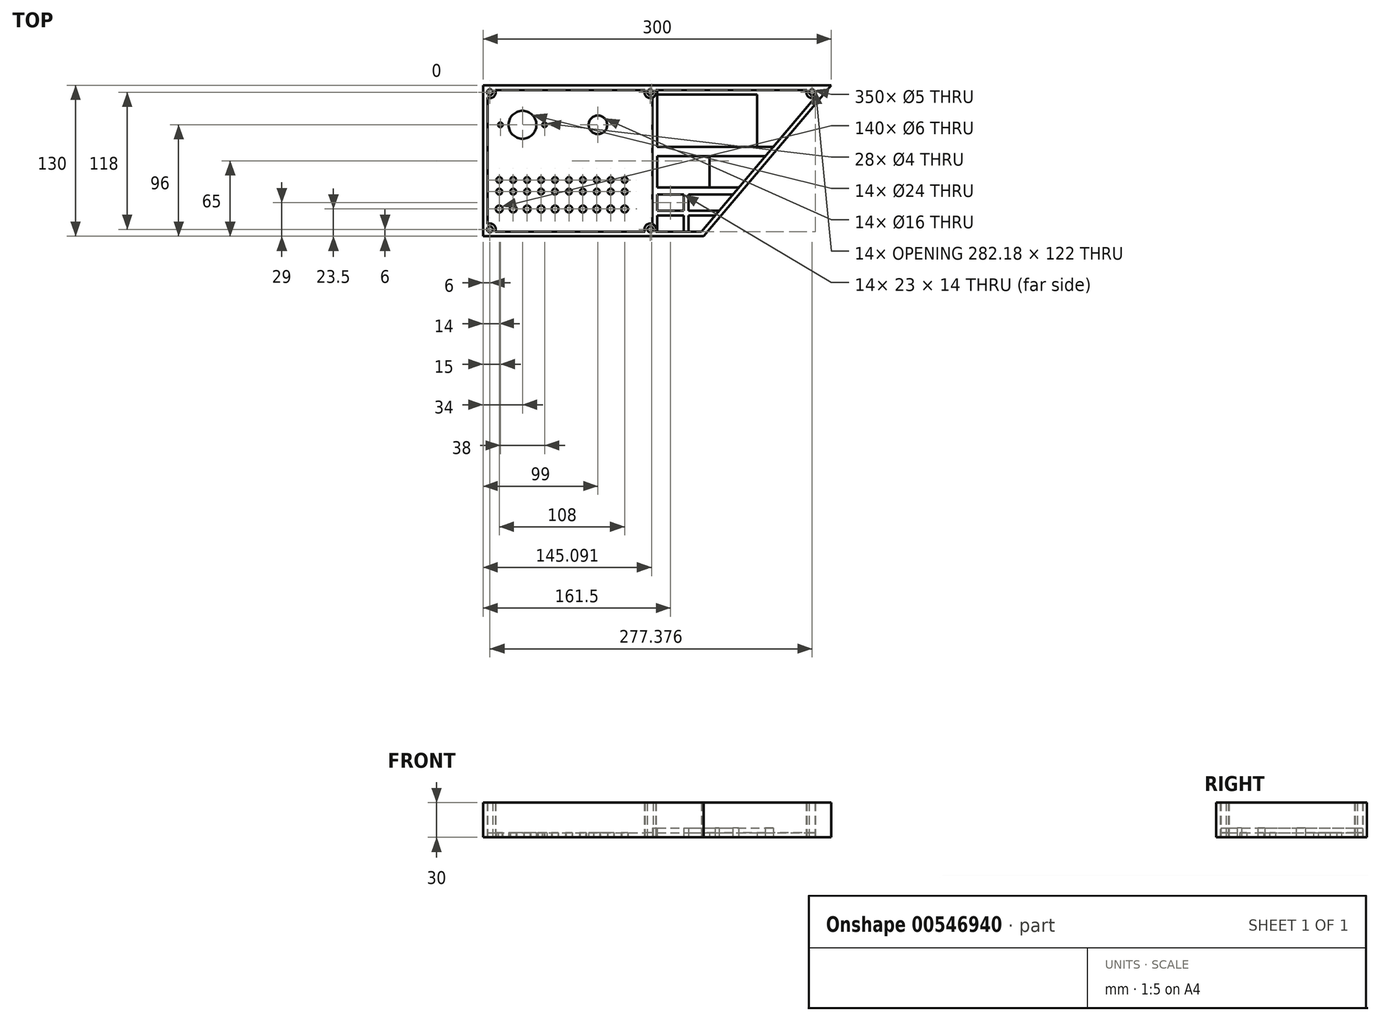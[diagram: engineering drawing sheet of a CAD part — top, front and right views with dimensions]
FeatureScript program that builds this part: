
annotation { "Feature Type Name" : "Feature", "Feature Type Description" : "" }
export const myFeature = defineFeature(function(context is Context, id is Id, definition is map)
    precondition{}
    {
        {
            var Q0;
            Q0=qCreatedBy(makeId("Top.planeOp"),FACE);
            var sketch = newSketch(context, id + "F0", { "sketchPlane" : qUnion([Q0])});
            skLineSegment(sketch, "E0", {"start": v(0, 0) * mm, "end": v(190, 0) * mm});
            skLineSegment(sketch, "E1", {"start": v(0, 0) * mm, "end": v(0, 130) * mm});
            skLineSegment(sketch, "E2", {"start": v(0, 130) * mm, "end": v(300, 130) * mm});
            skLineSegment(sketch, "E3", {"start": v(300, 130) * mm, "end": v(190, 0) * mm});
            skLineSegment(sketch, "E4.0", {"start": v(236, 77) * mm, "end": v(236, 122) * mm});
            skLineSegment(sketch, "E5.trimOffspring", {"start": v(195, 42) * mm, "end": v(195, 69) * mm});
            skLineSegment(sketch, "E6.0", {"start": v(173, 4) * mm, "end": v(173, 18) * mm});
            skLineSegment(sketch, "E7.0", {"start": v(150, 122) * mm, "end": v(236, 122) * mm});
            skLineSegment(sketch, "E8.0", {"start": v(150, 77) * mm, "end": v(249.91, 77) * mm});
            skLineSegment(sketch, "E9.0", {"start": v(150, 69) * mm, "end": v(243.14, 69) * mm});
            skLineSegment(sketch, "E10.0", {"start": v(150, 42) * mm, "end": v(220.3, 42) * mm});
            skLineSegment(sketch, "E11.0", {"start": v(150, 4) * mm, "end": v(173, 4) * mm});
            skLineSegment(sketch, "E12.0", {"start": v(150, 18) * mm, "end": v(173, 18) * mm});
            skLineSegment(sketch, "E13.0", {"start": v(150, 36) * mm, "end": v(173, 36) * mm});
            skLineSegment(sketch, "E14.0", {"start": v(150, 22) * mm, "end": v(173, 22) * mm});
            skLineSegment(sketch, "E15.trimOffspring", {"start": v(173, 22) * mm, "end": v(173, 36) * mm});
            skLineSegment(sketch, "E16.0", {"start": v(10.58, 126) * mm, "end": v(139.42, 126) * mm});
            skLineSegment(sketch, "E17.0", {"start": v(286.18, 119.86) * mm, "end": v(188.14, 4) * mm});
            skLineSegment(sketch, "E18.0", {"start": v(10.58, 4) * mm, "end": v(139.42, 4) * mm});
            skLineSegment(sketch, "E19.0", {"start": v(4, 10.58) * mm, "end": v(4, 119.42) * mm});
            skLineSegment(sketch, "E20", {"start": v(150, 4) * mm, "end": v(150, 126) * mm});
            skLineSegment(sketch, "E21.0", {"start": v(146, 10.58) * mm, "end": v(146, 119.42) * mm});
            skLineSegment(sketch, "E22.0", {"start": v(177, 22) * mm, "end": v(177, 36) * mm});
            skLineSegment(sketch, "E23.0", {"start": v(177, 4) * mm, "end": v(177, 18) * mm});
            skLineSegment(sketch, "E24.trimOffspring", {"start": v(177, 36) * mm, "end": v(215.22, 36) * mm});
            skLineSegment(sketch, "E25.trimOffspring", {"start": v(177, 22) * mm, "end": v(203.38, 22) * mm});
            skLineSegment(sketch, "E26.trimOffspring", {"start": v(177, 18) * mm, "end": v(200, 18) * mm});
            skLineSegment(sketch, "E27", {"start": v(10.58, 126) * mm, "end": v(34, 126) * mm, "construction": true});
            skLineSegment(sketch, "E28", {"start": v(34, 126) * mm, "end": v(34, 96) * mm, "construction": true});
            skCircle(sketch, "E29", {"center": v(34, 96) * mm, "radius": 12 * mm});
            skLineSegment(sketch, "E30.0", {"start": v(15, 126) * mm, "end": v(15, 96) * mm, "construction": true});
            skLineSegment(sketch, "E31.0", {"start": v(53, 126) * mm, "end": v(53, 96) * mm, "construction": true});
            skCircle(sketch, "E32", {"center": v(15, 96) * mm, "radius": 2 * mm});
            skCircle(sketch, "E33", {"center": v(53, 96) * mm, "radius": 2 * mm});
            skCircle(sketch, "E34", {"center": v(34, 96) * mm, "radius": 30 * mm, "construction": true});
            skLineSegment(sketch, "E35.0", {"start": v(4, 23.5) * mm, "end": v(146, 23.5) * mm, "construction": true});
            skLineSegment(sketch, "E36.0", {"start": v(4, 38.5) * mm, "end": v(146, 38.5) * mm, "construction": true});
            skLineSegment(sketch, "E37.0", {"start": v(4, 49) * mm, "end": v(146, 49) * mm, "construction": true});
            skLineSegment(sketch, "E38", {"start": v(4, 10.58) * mm, "end": v(4, 49) * mm, "construction": true});
            skLineSegment(sketch, "E39.0", {"start": v(14, 3.5) * mm, "end": v(14, 23.5) * mm, "construction": true});
            skLineSegment(sketch, "E40.0", {"start": v(26, 3.5) * mm, "end": v(26, 23.5) * mm, "construction": true});
            skLineSegment(sketch, "E41.0", {"start": v(38, 3.5) * mm, "end": v(38, 23.5) * mm, "construction": true});
            skLineSegment(sketch, "E42.0", {"start": v(50, 3.5) * mm, "end": v(50, 23.5) * mm, "construction": true});
            skLineSegment(sketch, "E43.0", {"start": v(62, 3.5) * mm, "end": v(62, 23.5) * mm, "construction": true});
            skLineSegment(sketch, "E44.0", {"start": v(74, 3.5) * mm, "end": v(74, 23.5) * mm, "construction": true});
            skLineSegment(sketch, "E45.0", {"start": v(86, 3.5) * mm, "end": v(86, 23.5) * mm, "construction": true});
            skLineSegment(sketch, "E46.0", {"start": v(98, 3.5) * mm, "end": v(98, 23.5) * mm, "construction": true});
            skLineSegment(sketch, "E47.0", {"start": v(110, 3.5) * mm, "end": v(110, 23.5) * mm, "construction": true});
            skLineSegment(sketch, "E48.0", {"start": v(122, 3.5) * mm, "end": v(122, 23.5) * mm, "construction": true});
            skLineSegment(sketch, "E49.trimOffspring", {"start": v(122, 38.5) * mm, "end": v(122, 48.5) * mm, "construction": true});
            skLineSegment(sketch, "E50.trimOffspring", {"start": v(110, 38.5) * mm, "end": v(110, 48.5) * mm, "construction": true});
            skLineSegment(sketch, "E51.trimOffspring", {"start": v(98, 38.5) * mm, "end": v(98, 48.5) * mm, "construction": true});
            skLineSegment(sketch, "E52.trimOffspring", {"start": v(86, 38.5) * mm, "end": v(86, 48.5) * mm, "construction": true});
            skLineSegment(sketch, "E53.trimOffspring", {"start": v(74, 38.5) * mm, "end": v(74, 48.5) * mm, "construction": true});
            skLineSegment(sketch, "E54.trimOffspring", {"start": v(62, 38.5) * mm, "end": v(62, 48.5) * mm, "construction": true});
            skLineSegment(sketch, "E55.trimOffspring", {"start": v(50, 38.5) * mm, "end": v(50, 48.5) * mm, "construction": true});
            skLineSegment(sketch, "E56.trimOffspring", {"start": v(38, 38.5) * mm, "end": v(38, 48.5) * mm, "construction": true});
            skLineSegment(sketch, "E57.trimOffspring", {"start": v(26, 38.5) * mm, "end": v(26, 48.5) * mm, "construction": true});
            skLineSegment(sketch, "E58.trimOffspring", {"start": v(14, 38.5) * mm, "end": v(14, 48.5) * mm, "construction": true});
            skCircle(sketch, "E59", {"center": v(14, 23.5) * mm, "radius": 3 * mm});
            skCircle(sketch, "E60", {"center": v(26, 23.5) * mm, "radius": 3 * mm});
            skCircle(sketch, "E61", {"center": v(38, 23.5) * mm, "radius": 3 * mm});
            skCircle(sketch, "E62", {"center": v(50, 23.5) * mm, "radius": 3 * mm});
            skCircle(sketch, "E63", {"center": v(62, 23.5) * mm, "radius": 3 * mm});
            skCircle(sketch, "E64", {"center": v(74, 23.5) * mm, "radius": 3 * mm});
            skCircle(sketch, "E65", {"center": v(86, 23.5) * mm, "radius": 3 * mm});
            skCircle(sketch, "E66", {"center": v(98, 23.5) * mm, "radius": 3 * mm});
            skCircle(sketch, "E67", {"center": v(110, 23.5) * mm, "radius": 3 * mm});
            skCircle(sketch, "E68", {"center": v(122, 23.5) * mm, "radius": 3 * mm});
            skCircle(sketch, "E69", {"center": v(14, 38.5) * mm, "radius": 2.5 * mm});
            skCircle(sketch, "E70", {"center": v(26, 38.5) * mm, "radius": 2.5 * mm});
            skCircle(sketch, "E71", {"center": v(38, 38.5) * mm, "radius": 2.5 * mm});
            skCircle(sketch, "E72", {"center": v(50, 38.5) * mm, "radius": 2.5 * mm});
            skCircle(sketch, "E73", {"center": v(62, 38.5) * mm, "radius": 2.5 * mm});
            skCircle(sketch, "E74", {"center": v(74, 38.5) * mm, "radius": 2.5 * mm});
            skCircle(sketch, "E75", {"center": v(86, 38.5) * mm, "radius": 2.5 * mm});
            skCircle(sketch, "E76", {"center": v(98, 38.5) * mm, "radius": 2.5 * mm});
            skCircle(sketch, "E77", {"center": v(110, 38.5) * mm, "radius": 2.5 * mm});
            skCircle(sketch, "E78", {"center": v(122, 38.5) * mm, "radius": 2.5 * mm});
            skCircle(sketch, "E79", {"center": v(14, 48.5) * mm, "radius": 2.5 * mm});
            skCircle(sketch, "E80", {"center": v(26, 48.5) * mm, "radius": 2.5 * mm});
            skCircle(sketch, "E81", {"center": v(38, 48.5) * mm, "radius": 2.5 * mm});
            skCircle(sketch, "E82", {"center": v(50, 48.5) * mm, "radius": 2.5 * mm});
            skCircle(sketch, "E83", {"center": v(62, 48.5) * mm, "radius": 2.5 * mm});
            skCircle(sketch, "E84", {"center": v(74, 48.5) * mm, "radius": 2.5 * mm});
            skCircle(sketch, "E85", {"center": v(86, 48.5) * mm, "radius": 2.5 * mm});
            skCircle(sketch, "E86", {"center": v(98, 48.5) * mm, "radius": 2.5 * mm});
            skCircle(sketch, "E87", {"center": v(110, 48.5) * mm, "radius": 2.5 * mm});
            skCircle(sketch, "E88", {"center": v(122, 48.5) * mm, "radius": 2.5 * mm});
            skLineSegment(sketch, "E89", {"start": v(34, 96) * mm, "end": v(99, 96) * mm, "construction": true});
            skCircle(sketch, "E90", {"center": v(99, 96) * mm, "radius": 8 * mm});
            skCircle(sketch, "E91", {"center": v(6, 124) * mm, "radius": 2.5 * mm});
            skArc(sketch, "E92", {"start": v(4, 119.42) * mm, "mid": v(9.54, 120.46) * mm, "end": v(10.58, 126) * mm});
            skCircle(sketch, "E93", {"center": v(6, 6) * mm, "radius": 2.5 * mm});
            skArc(sketch, "E94", {"start": v(10.58, 4) * mm, "mid": v(9.54, 9.54) * mm, "end": v(4, 10.58) * mm});
            skLineSegment(sketch, "E95", {"start": v(146, 6) * mm, "end": v(144, 6) * mm, "construction": true});
            skCircle(sketch, "E96", {"center": v(144, 6) * mm, "radius": 2.5 * mm});
            skArc(sketch, "E97", {"start": v(148.58, 4) * mm, "mid": v(144, 11) * mm, "end": v(139.42, 4) * mm});
            skPoint(sketch, "E98.orphan", {"position": v(146, 4) * mm});
            skLineSegment(sketch, "E99.trimOffspring", {"start": v(148.58, 4) * mm, "end": v(188.14, 4) * mm});
            skCircle(sketch, "E100", {"center": v(144, 124) * mm, "radius": 2.5 * mm});
            skArc(sketch, "E101", {"start": v(139.42, 126) * mm, "mid": v(144, 119) * mm, "end": v(148.58, 126) * mm});
            skLineSegment(sketch, "E102.trimOffspring", {"start": v(148.58, 126) * mm, "end": v(278.8, 126) * mm});
            skLineSegment(sketch, "E103", {"start": v(283.38, 122) * mm, "end": v(283.38, 124) * mm, "construction": true});
            skCircle(sketch, "E104", {"center": v(283.38, 124) * mm, "radius": 2.5 * mm});
            skArc(sketch, "E105", {"start": v(278.8, 126) * mm, "mid": v(280.18, 120.15) * mm, "end": v(286.18, 119.86) * mm});
            skSolve(sketch);
        }
        {
            var Q0;
            {var subQ6=sQuery(id+"F0.wireOp",EDGE,"E4.0");Q0=makeQuery(id+"F0.imprint","IMPRINT",FACE,{"disambiguationData":[TD([[makeQuery(id+"F0.imprint","IMPRINT",EDGE,{"derivedFrom":subQ6}),-1.0]])]});}
            var Q1;
            {var subQ0=sQuery(id+"F0.wireOp",EDGE,"E5.trimOffspring");Q1=makeQuery(id+"F0.imprint","IMPRINT",FACE,{"disambiguationData":[TD([[makeQuery(id+"F0.imprint","IMPRINT",EDGE,{"derivedFrom":subQ0}),-1.0]])]});}
            var Q2;
            Q2=makeQuery(id+"F0.imprint","IMPRINT",FACE,{"disambiguationData":[TD([[makeQuery(id+"F0.imprint","IMPRINT",EDGE,{"derivedFrom":sQuery(id+"F0.wireOp",EDGE,"E22.0")}),-1.0]])]});
            var Q3;
            {var subQ4=sQuery(id+"F0.wireOp",EDGE,"E23.0");Q3=makeQuery(id+"F0.imprint","IMPRINT",FACE,{"disambiguationData":[TD([[makeQuery(id+"F0.imprint","IMPRINT",EDGE,{"derivedFrom":subQ4}),-1.0]])]});}
            var Q4;
            {var subQ0=sQuery(id+"F0.wireOp",EDGE,"E19.0");Q4=makeQuery(id+"F0.imprint","IMPRINT",FACE,{"disambiguationData":[TD([[makeQuery(id+"F0.imprint","IMPRINT",EDGE,{"derivedFrom":subQ0}),-1.0]])]});}
            extrude(context, id + "F1", {"entities" : qUnion([Q0, Q1, Q2, Q3, Q4]), "depth" : 4 * mm, "offsetDistance" : 25 * mm});
        }
        {
            var Q0;
            {var subQ4=sQuery(id+"F0.wireOp",EDGE,"E8.0");var subQ8=makeQuery(id+"F0.imprint","INTERSECT",VERTEX,{"derivedFrom":[sQuery(id+"F0.wireOp",EDGE,"E4.0"),subQ4]});Q0=makeQuery(id+"F0.imprint","IMPRINT",FACE,{"disambiguationData":[TD([[makeQuery(id+"F0.imprint","IMPRINT",EDGE,{"disambiguationData":[TD([[subQ8,1.0]])],"derivedFrom":subQ4}),-1.0]])]});}
            var Q1;
            {var subQ9=sQuery(id+"F0.wireOp",EDGE,"E21.0");Q1=makeQuery(id+"F0.imprint","IMPRINT",FACE,{"disambiguationData":[TD([[makeQuery(id+"F0.imprint","IMPRINT",EDGE,{"derivedFrom":subQ9}),-1.0]])]});}
            var Q2;
            {var subQ1=sQuery(id+"F0.wireOp",EDGE,"E6.0");Q2=makeQuery(id+"F0.imprint","IMPRINT",FACE,{"disambiguationData":[TD([[makeQuery(id+"F0.imprint","IMPRINT",EDGE,{"derivedFrom":subQ1}),-1.0]])]});}
            extrude(context, id + "F2", {"entities" : qUnion([Q0, Q1, Q2]), "depth" : 8 * mm, "offsetDistance" : 25 * mm});
        }
        {
            var Q0;
            Q0=makeQuery(id+"F0.imprint","IMPRINT",FACE,{"disambiguationData":[TD([[makeQuery(id+"F0.imprint","IMPRINT",EDGE,{"derivedFrom":sQuery(id+"F0.wireOp",EDGE,"E0")}),1.0]])]});
            extrude(context, id + "F3", {"entities" : qUnion([Q0]), "depth" : 30 * mm, "offsetDistance" : 25 * mm});
        }
    });
